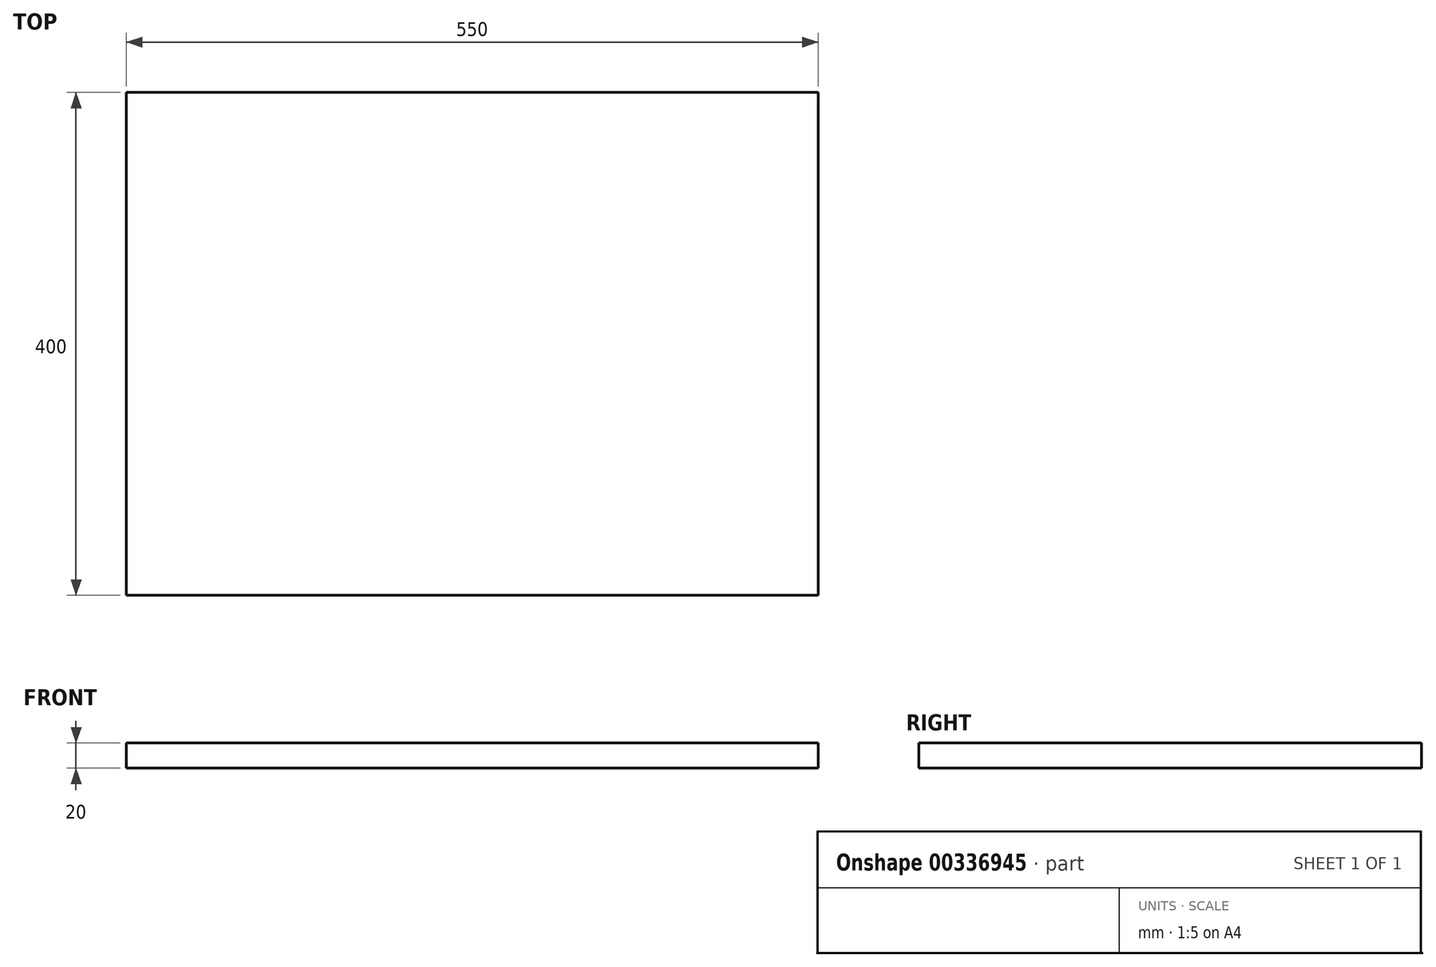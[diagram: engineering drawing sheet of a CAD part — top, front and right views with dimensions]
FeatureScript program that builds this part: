
annotation { "Feature Type Name" : "Feature", "Feature Type Description" : "" }
export const myFeature = defineFeature(function(context is Context, id is Id, definition is map)
    precondition{}
    {
        {
            var Q0;
            Q0=qCreatedBy(makeId("Top.planeOp"),FACE);
            var sketch = newSketch(context, id + "F0", { "sketchPlane" : qUnion([Q0])});
            skLineSegment(sketch, "E0.bottom", {"start": v(-275.1, 259.6) * mm, "end": v(274.9, 259.6) * mm});
            skLineSegment(sketch, "E0.top", {"start": v(-275.1, -140.4) * mm, "end": v(274.9, -140.4) * mm});
            skLineSegment(sketch, "E0.left", {"start": v(-275.1, 259.6) * mm, "end": v(-275.1, -140.4) * mm});
            skLineSegment(sketch, "E0.right", {"start": v(274.9, 259.6) * mm, "end": v(274.9, -140.4) * mm});
            skSolve(sketch);
        }
        {
            var Q0;
            Q0=makeQuery(id+"F0.imprint","IMPRINT",FACE,{"disambiguationData":[TD([[makeQuery(id+"F0.imprint","IMPRINT",EDGE,{"derivedFrom":sQuery(id+"F0.wireOp",EDGE,"E0.bottom")}),-1.0]])]});
            extrude(context, id + "F1", {"entities" : qUnion([Q0]), "depth" : 20 * mm});
        }
    });
